# Revit family: Gira_104600
name_source: partatom
category: Electrical Fixtures
revit_build: Autodesk Revit 2017 (Build: 20160225_1515(x64)
units: mm (PartAtom-declared; Revit-internal decimal feet)

## family parameters
Cut with Voids When Loaded = No
Host = Face
Maintain Annotation Orientation = No
Part Type = Normal
Room Calculation Point = No
Round Connector Dimension = Use Diameter
Shared = No

## types (1)
- Swit.act. 8-g 16 A man.act. + C-load KNX DRA
    BIM = https://media.live.bim.site 16f.rfa
    BIMSITE_PRODUCT_ID = a3e6c1ae2a3f1c518e88d64d5e62ebf619d153d8
    Bus connection included = Yes
    Cost = 0 $
    Default Elevation = 1219 mm
    Description = Swit.act.8g 16A C load DRA KNX KNX switching actuator, 8-gang 16 A with manual actuation and current measurement for C-loads,DRA plus DRA switching actuators with integrated bus coupler. For switching independently controllable groups of loads. With manual switch for switching over the relay (On Off) parallel or without KNX operation. Multi-phase connection. No additional power supply required.,Features: - Manual actuation of the relay independent of the bus or switching position indication. - NO contact or NC contact operation. - Central switching function. - Group feedback for reduction of bus load. - Active or passive (object can be read out) cyclical feedback function. - Feedback can be delayed until after the recovery of bus voltage. - Logical linking function for each output. - Block function can be parameterised for each channel. As an alternative, forced setting function for each output. - Time functions (switch-on off delay, staircase light function – also with advance warning function). - Integration in light scenes is possible, eight internal scenes at the most can be parameterised per channel. - Memory function for light scenes. - Elapsed operating time meter as forward backward counter with limit function (limit can be changed via bus) can be activated for each output. - Input monitoring for cyclical updating with safety setting. - Reactions in case of bus voltage failure and restoration can be set for each channel following an ETS programming process. - The switching contacts of the switching actuator, 8-gang, C-load are especially designed for loads with a capacitive character, and therefore conditional, brief, high switch-on currents (see Technical Data). - The switching actuator has an integrated current detection. - A current measurement can be carried out for each channel. - Current detection: Measurement of load current for each channel. - Threshold values for load monitoring (e.g. signalling of load failure). - Independent switching of the eight outputs.,Notes : - Installation on DIN top-hat rail. - VDE approval in accordance with EN 60669-1, EN 60669-2-1.
    GTIN = 4010337042273
    HAN = 104600
    HeinzeBIM = https://www.heinze.de
    Local operation/hand operation = Yes
    Manufacturer = Gira
    Rated current [Ampere] = 16
    Suitable for C-load = Yes
    URL = https://www.gira.de

## geometry (parser evidence)
native form markers: Blend x2, Sweep x3
no freeform markers — native parametric forms only
